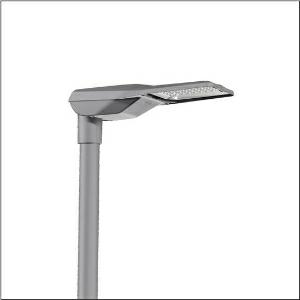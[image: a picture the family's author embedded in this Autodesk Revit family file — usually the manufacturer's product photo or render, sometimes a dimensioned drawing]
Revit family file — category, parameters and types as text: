
# Revit family: streetlight_sl_21_iq_mini___st1_0ab_5xe2m31d08hb_2a38
name_source: partatom
category: Lighting Fixtures
units: mm (PartAtom-declared; Revit-internal decimal feet)

## family parameters
Cut with Voids When Loaded = No
Host = Face
Light Source = No
Part Type = Normal
Room Calculation Point = No
Round Connector Dimension = Use Diameter
Shared = No

## types (1)
- --- (1 x LED, 8320 lm, 70.9 W, 3000K)
    Apparent Load = 71 VA
    CIE Flux Codes = 38 73 97 100 100
    Color Rendering = 70
    Color Temperature = 3000K
    Default Elevation = 1800 mm
    Description = Streetlight SL 21 iQ mini, mast luminaire, primary light control with lens, of PMMA, primary optical cover: cover, of toughened safety glass, transparent, light distribution: ST1.0aB, light emission: direct distribution, primary light characteristic: asymmetric, installation type: post-top, side-entry, LED, High Power LED, rated luminous flux: 8.320lm, luminous efficacy: 117lm/W, light colour: 730, colour temperature: 3000K, control gear: iQ-Comfort, control: Auto-Match, Temp-Guard, Lumen-Switch, Night-Set, Smart-Wire, Light-Fading, Desk-Remote (wireless, voltage-free reading and setting of iQ features in the workshop via application-optimized NFC function/RFID function), optimised constant luminous flux control (CLO 2.0), pre-setting: linear dimming characteristic, mains connection: 220..240V, AC, 50/60Hz, start of lifetime: 71W, end of service life: 75W, reduction: 31W, luminaire housing, of diecast aluminium, powder-coated, SITECO metallic grey (DB 702S), corrosivity category C5 high according to DIN EN ISO 12944, please order mast flange separately, inclination adjustable: 0°, 5°, 10°, 15°, sealing non-destructively replaceable, multi-level sealing system, length: 628mm, width: 235mm, height: 110mm, mast flange for spigot size: 42mm (side-entry): 5XC10008XM4, 60/48mm (side-entry/post-top): 5XC10108XM2, 76/60mm (side-entry/post-top): 5XC10108XM1, mounting height: 4..8m, protection rating (complete): IP66, insulation class (complete): insulation class II (safety insulation), certification: CE, ENEC, ENEC+, VDE, impact resistance: IK10, permissible operating ambient temperature for outdoor applications: -40..+50°C, standard-compliant lighting for roads and squares, packaging unit: 1 piece

Light Distribution: ST1.0aB
    Height = 110 mm
    Lamp = 1 x LED
    Lamp Light Flux = 8320 lm
    Lamp Power = 70.9 W
    Lamp count = 1
    Length = 625 mm
    Luminous efficacy = 117 lm/W
    Manufacturer = Siteco
    ModVariant = No
    Model = 5XE2M31D08HB
    Number of Poles = 1
    OnlyDefault = Yes
    Power Factor = 1
    Product Name = Streetlight SL 21 iQ mini | ST1.0aB
    Product group = mast luminaire | pylon top
    ProductGroupID = 6100
    Protection Class = Protection class II
    Protection Degree = IP 66
    RLX_Detail_Level = 1
    RLX_Emergency_Light_Flux = 0 lm
    RLX_Emergency_Type = 0
    RLX_Emergency_Type_DB = No
    RlxData = <blob elided: 26281 chars, md5=b4029885>
    Socket = socket
    Standby Power = 0 W
    System Light Flux = 8320 lm
    System Power = 71 W
    Type Comments = factory setting: luminous flux: 100 % | dim-lin: 254 | 711 mA
    Type Image = l_1003519.jpg
    URL = http://relux.com
    VarID = @adj_156653
    Voltage = 0 V
    Weight = 0.00 kg
    Width = 234 mm

## geometry (parser evidence)
native form markers: Blend x4, Sweep x12
no freeform markers — native parametric forms only
